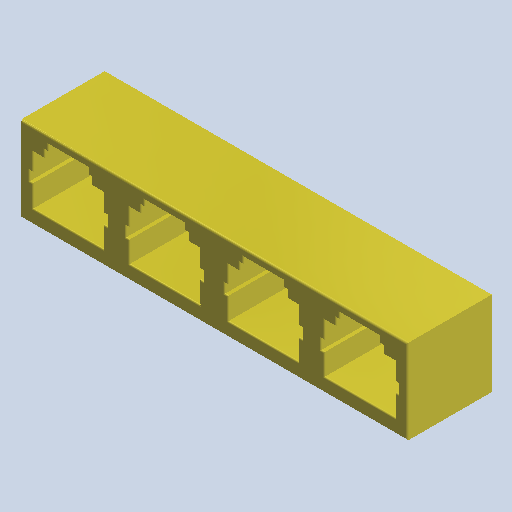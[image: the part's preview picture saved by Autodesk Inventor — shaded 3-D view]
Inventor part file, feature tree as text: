
AUTODESK INVENTOR PART (.ipt)
format: ipt  version: 2022.1 (Build 261234000, 234)  size: 343,552 bytes
history: mixed  units: mm (DEFAULTED — no unit token found)
features: other x8, fillet x1, imported_body x1
bodies: Body1 (imported_parasolid)
feature tree (10):
  other  "Sólido1"
  other  "Origen"
  other  "Plano YZ"
  other  "Plano XZ"
  other  "Plano XY"
  other  "Eje X"
  other  "Eje Y"
  other  "Eje Z"
  fillet  "Fillet2"  [1 undecoded]
  imported_body  NMx_Import_Brep_tag  [imported B-rep: ~434 faces, bbox_mm=[55.0, 12.0, 12.0]]
note: 1 required parameter value undecoded (feature->parameter linkage not recoverable at this tier; creation-order binding heuristic only, values carry confidence <= 0.55)
